# Revit family: Kohler Strayt 37335IN-4FP-CP Family
name_source: partatom
category: Generic Models
revit_build: Autodesk Revit 2018 (Build: 20170223_1515(x64)
units: mm (PartAtom-declared; Revit-internal decimal feet)

## family parameters
Can host rebar = No
Cut with Voids When Loaded = No
Host = Face
Part Type = Normal
Room Calculation Point = No
Round Connector Dimension = Use Diameter
Shared = No

## types (1)
- Kohler Strayt 37335IN-4FP-CP Family
    Default Elevation = 1219 mm
    Description = Strayt Recessed Bath & Shower Trim
    Disclamer = Although care has been taken to ensure, to the best of our knowledge, that all data and information contained herein is accurate
to the extent that it relates to either matters of fact or accepted practice at the time of issue. MDFC (Pty) Ltd assumes no responsibility for
any errors in, or misinterpretation of, such data and/ or information or any loss or damage arising from, or related to its use.
    Handle Height = 110 mm  [stored 0.360892 ft]
    Handle Length = 54 mm  [stored 0.177165 ft]
    Manufacturer = Kohler CO
    Material = Fauctes
    Model = 37335IN-4FP-CP
    Plate Height = 166 mm  [stored 0.544619 ft]
    Plate Length = 135 mm  [stored 0.442913 ft]
    Telephone = 011 050 9000
    URL = http://www.africa.kohler.com

note: [stored X ft] marks values corroborated as IEEE doubles in the binary element streams (Revit-internal decimal feet)

## geometry (parser evidence)
native form markers: Sweep x1
no freeform markers — native parametric forms only
